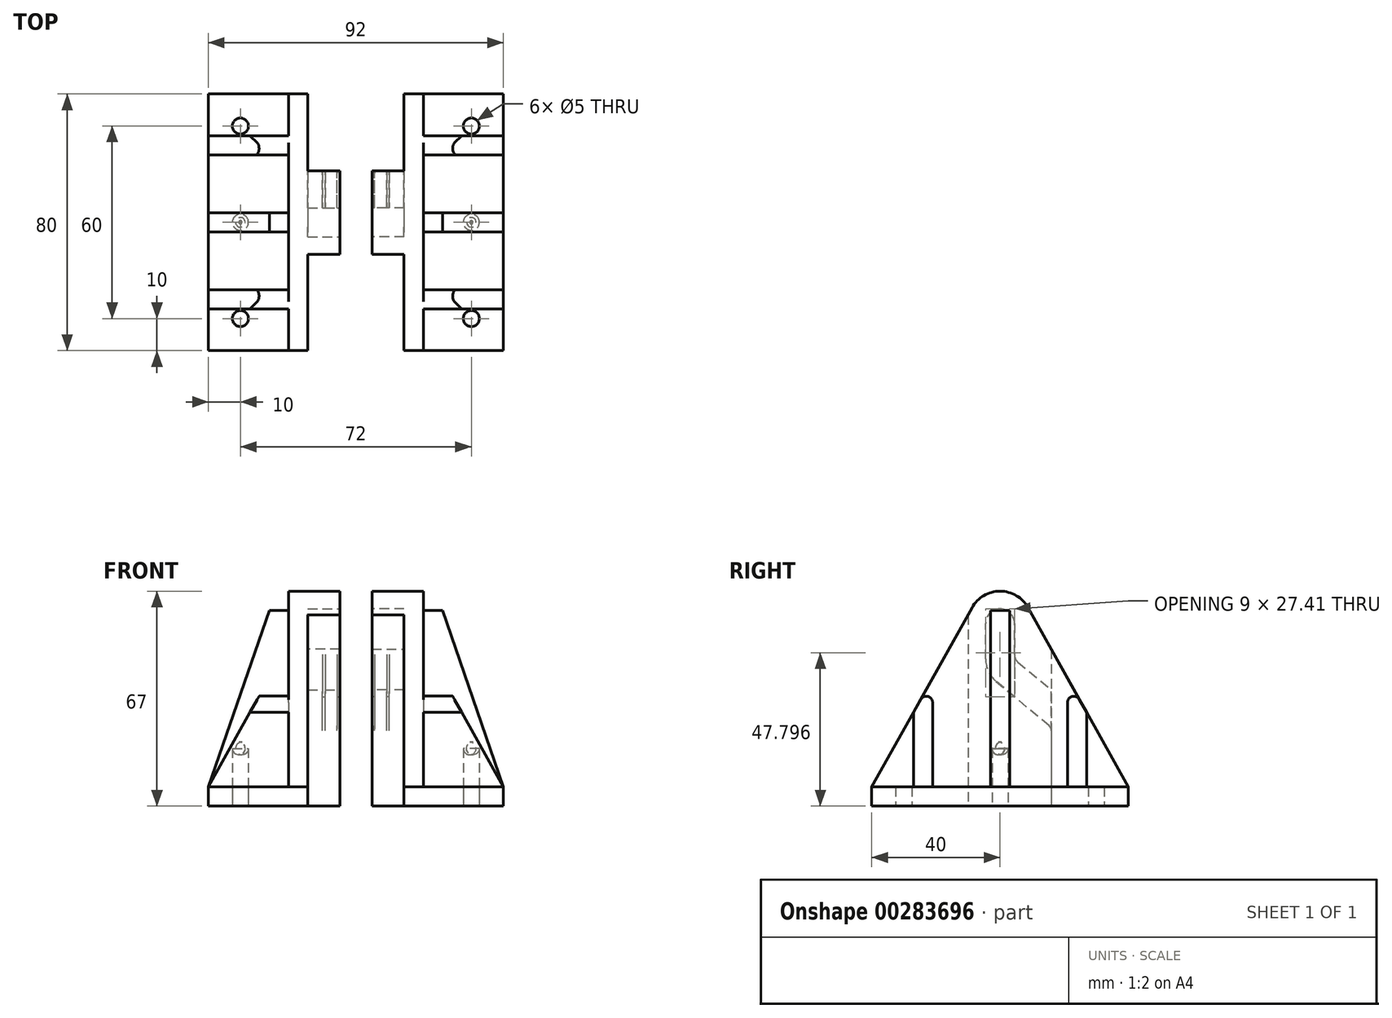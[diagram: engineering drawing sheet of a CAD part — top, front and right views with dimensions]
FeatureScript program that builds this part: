
annotation { "Feature Type Name" : "Feature", "Feature Type Description" : "" }
export const myFeature = defineFeature(function(context is Context, id is Id, definition is map)
    precondition{}
    {
        {
            var Q0;
            Q0=qCreatedBy(makeId("Top.planeOp"),FACE);
            var sketch = newSketch(context, id + "F0", { "sketchPlane" : qUnion([Q0])});
            skLineSegment(sketch, "E0.bottom", {"start": v(-15.5, 40) * mm, "end": v(15.5, 40) * mm});
            skLineSegment(sketch, "E0.top", {"start": v(-15.5, -40) * mm, "end": v(15.5, -40) * mm});
            skLineSegment(sketch, "E0.left", {"start": v(-15.5, 40) * mm, "end": v(-15.5, -40) * mm});
            skLineSegment(sketch, "E0.right", {"start": v(15.5, 40) * mm, "end": v(15.5, 16) * mm});
            skPoint(sketch, "E0.middle", {"position": v(0, 0) * mm});
            skLineSegment(sketch, "E1.bottom", {"start": v(15.5, 16) * mm, "end": v(25.5, 16) * mm});
            skLineSegment(sketch, "E1.top", {"start": v(15.5, -10) * mm, "end": v(25.5, -10) * mm});
            skLineSegment(sketch, "E1.right", {"start": v(25.5, 16) * mm, "end": v(25.5, -10) * mm});
            skLineSegment(sketch, "E2.trimOffspring", {"start": v(15.5, -10) * mm, "end": v(15.5, -40) * mm});
            skSolve(sketch);
        }
        {
            var Q0;
            Q0=makeQuery(id+"F0.imprint","IMPRINT",FACE,{"disambiguationData":[TD([[makeQuery(id+"F0.imprint","IMPRINT",EDGE,{"derivedFrom":sQuery(id+"F0.wireOp",EDGE,"E0.bottom")}),-1.0]])]});
            extrude(context, id + "F1", {"entities" : qUnion([Q0]), "depth" : 6 * mm});
        }
        {
            var Q0;
            Q0=makeQuery(id+"F1.opExtrude","CAP_FACE",FACE,{"disambiguationData":[OSD([sQuery(id+"F0.wireOp",EDGE,"E0.bottom"),sQuery(id+"F0.wireOp",EDGE,"E0.top"),sQuery(id+"F0.wireOp",EDGE,"E0.left"),sQuery(id+"F0.wireOp",EDGE,"E0.right"),sQuery(id+"F0.wireOp",EDGE,"E1.bottom"),sQuery(id+"F0.wireOp",EDGE,"E1.top"),sQuery(id+"F0.wireOp",EDGE,"E1.right"),sQuery(id+"F0.wireOp",EDGE,"E2.trimOffspring")])],"isStart":false});
            var sketch = newSketch(context, id + "F2", { "sketchPlane" : qUnion([Q0])});
            skLineSegment(sketch, "E3.bottom", {"start": v(15.5, 40) * mm, "end": v(9.5, 40) * mm});
            skLineSegment(sketch, "E3.top", {"start": v(15.5, -40) * mm, "end": v(9.5, -40) * mm});
            skLineSegment(sketch, "E3.left", {"start": v(15.5, 40) * mm, "end": v(15.5, -40) * mm});
            skLineSegment(sketch, "E3.right", {"start": v(9.5, 40) * mm, "end": v(9.5, -40) * mm});
            skSolve(sketch);
        }
        {
            var Q0;
            {var subQ3=sQuery(id+"F2.wireOp",EDGE,"E3.bottom");Q0=makeQuery(id+"F2.imprint","IMPRINT",FACE,{"disambiguationData":[TD([[makeQuery(id+"F2.imprint","IMPRINT",EDGE,{"derivedFrom":subQ3}),-1.0]])]});}
            extrude(context, id + "F3", {"entities" : qUnion([Q0]), "operationType" : NewBodyOperationType.ADD, "depth" : 61 * mm});
        }
        {
            var Q0;
            Q0=makeQuery(id+"F3.opExtrude","SWEPT_FACE",FACE,{"disambiguationData":[OSD([sQuery(id+"F2.wireOp",EDGE,"E3.right")])]});
            var sketch = newSketch(context, id + "F4", { "sketchPlane" : qUnion([Q0])});
            skCircle(sketch, "E4", {"center": v(0, 57) * mm, "radius": 4 * mm, "construction": true});
            skArc(sketch, "E5", {"start": v(8.73, 61.88) * mm, "mid": v(0, 67) * mm, "end": v(-8.73, 61.88) * mm});
            skLineSegment(sketch, "E6", {"start": v(-40, 6) * mm, "end": v(-8.73, 61.88) * mm});
            skLineSegment(sketch, "E7", {"start": v(40, 6) * mm, "end": v(8.73, 61.88) * mm});
            skLineSegment(sketch, "E8", {"start": v(-40, 6) * mm, "end": v(-55.29, 6) * mm});
            skLineSegment(sketch, "E9", {"start": v(-55.29, 6) * mm, "end": v(-55.29, 71.33) * mm});
            skLineSegment(sketch, "E10", {"start": v(-55.29, 71.33) * mm, "end": v(42.45, 71.33) * mm});
            skLineSegment(sketch, "E11", {"start": v(42.45, 71.33) * mm, "end": v(40, 6) * mm});
            skSolve(sketch);
        }
        {
            var Q0;
            Q0 = qSketchRegion(id + "F4", true);
            extrude(context, id + "F5", {"entities" : qUnion([Q0]), "operationType" : NewBodyOperationType.REMOVE, "oppositeDirection" : true, "depth" : 25 * mm});
        }
        {
            var Q0;
            {var subQ0=sQuery(id+"F0.wireOp",EDGE,"E0.left");var subQ1=sQuery(id+"F0.wireOp",EDGE,"E0.top");var subQ2=sQuery(id+"F0.wireOp",EDGE,"E0.bottom");Q0=makeQuery(id+"F3.boolean.opBoolean","SPLIT",FACE,{"disambiguationData":[TD([makeQuery(id+"F1.opExtrude","SWEPT_FACE",FACE,{"disambiguationData":[OSD([subQ2])]})])],"derivedFrom":makeQuery(id+"F1.opExtrude","CAP_FACE",FACE,{"disambiguationData":[OSD([subQ2,subQ1,subQ0,sQuery(id+"F0.wireOp",EDGE,"E0.right"),sQuery(id+"F0.wireOp",EDGE,"E1.bottom"),sQuery(id+"F0.wireOp",EDGE,"E1.top"),sQuery(id+"F0.wireOp",EDGE,"E1.right"),sQuery(id+"F0.wireOp",EDGE,"E2.trimOffspring")])],"isStart":false})});}
            var sketch = newSketch(context, id + "F6", { "sketchPlane" : qUnion([Q0])});
            skLineSegment(sketch, "E12.bottom", {"start": v(-15.5, 3) * mm, "end": v(9.5, 3) * mm});
            skLineSegment(sketch, "E12.top", {"start": v(-15.5, -3) * mm, "end": v(9.5, -3) * mm});
            skLineSegment(sketch, "E12.left", {"start": v(-15.5, 3) * mm, "end": v(-15.5, -3) * mm});
            skLineSegment(sketch, "E12.right", {"start": v(9.5, 3) * mm, "end": v(9.5, -3) * mm});
            skLineSegment(sketch, "E13.bottom", {"start": v(-15.5, -21) * mm, "end": v(9.5, -21) * mm});
            skLineSegment(sketch, "E13.top", {"start": v(-15.5, -27) * mm, "end": v(9.5, -27) * mm});
            skLineSegment(sketch, "E13.left", {"start": v(-15.5, -21) * mm, "end": v(-15.5, -27) * mm});
            skLineSegment(sketch, "E13.right", {"start": v(9.5, -21) * mm, "end": v(9.5, -27) * mm});
            skLineSegment(sketch, "E14.bottom", {"start": v(-15.5, 27) * mm, "end": v(9.5, 27) * mm});
            skLineSegment(sketch, "E14.top", {"start": v(-15.5, 21) * mm, "end": v(9.5, 21) * mm});
            skLineSegment(sketch, "E14.left", {"start": v(-15.5, 27) * mm, "end": v(-15.5, 21) * mm});
            skLineSegment(sketch, "E14.right", {"start": v(9.5, 27) * mm, "end": v(9.5, 21) * mm});
            skSolve(sketch);
        }
        {
            var Q0;
            Q0 = qSketchRegion(id + "F6", true);
            extrude(context, id + "F7", {"entities" : qUnion([Q0]), "operationType" : NewBodyOperationType.ADD, "depth" : 55 * mm});
        }
        {
            var Q0;
            Q0=makeQuery(id+"F7.opExtrude","SWEPT_FACE",FACE,{"disambiguationData":[OSD([sQuery(id+"F6.wireOp",EDGE,"E13.right")])]});
            var sketch = newSketch(context, id + "F8", { "sketchPlane" : qUnion([Q0])});
            skLineSegment(sketch, "E15.0", {"start": v(-40, 6) * mm, "end": v(-27, 29.23) * mm});
            skLineSegment(sketch, "E15.1", {"start": v(-27, 29.23) * mm, "end": v(-21, 39.95) * mm});
            skLineSegment(sketch, "E15.2", {"start": v(-21, 39.95) * mm, "end": v(-8.73, 61.88) * mm});
            skArc(sketch, "E15.3", {"start": v(-8.73, 61.88) * mm, "mid": v(-6.3, 64.76) * mm, "end": v(-3, 66.54) * mm});
            skArc(sketch, "E15.4", {"start": v(-3, 66.54) * mm, "mid": v(0, 67) * mm, "end": v(3, 66.54) * mm});
            skArc(sketch, "E15.5", {"start": v(3, 66.54) * mm, "mid": v(6.3, 64.76) * mm, "end": v(8.73, 61.88) * mm});
            skLineSegment(sketch, "E15.6", {"start": v(21, 39.95) * mm, "end": v(8.73, 61.88) * mm});
            skLineSegment(sketch, "E15.7", {"start": v(27, 29.23) * mm, "end": v(21, 39.95) * mm});
            skLineSegment(sketch, "E15.8", {"start": v(40, 6) * mm, "end": v(27, 29.23) * mm});
            skLineSegment(sketch, "E16", {"start": v(-40, 6) * mm, "end": v(-71.4, 87.62) * mm});
            skLineSegment(sketch, "E17", {"start": v(-71.4, 87.62) * mm, "end": v(67.9, 87.62) * mm});
            skLineSegment(sketch, "E18", {"start": v(67.9, 87.62) * mm, "end": v(40, 6) * mm});
            skSolve(sketch);
        }
        {
            var Q0;
            Q0 = qSketchRegion(id + "F8", true);
            extrude(context, id + "F9", {"entities" : qUnion([Q0]), "operationType" : NewBodyOperationType.REMOVE, "oppositeDirection" : true, "depth" : 66 * mm});
        }
        {
            var Q0;
            Q0=makeQuery(id+"F3.boolean.opBoolean","MERGE",FACE,{"derivedFrom":[makeQuery(id+"F1.opExtrude","SWEPT_FACE",FACE,{"disambiguationData":[OSD([sQuery(id+"F0.wireOp",EDGE,"E0.right")])]}),makeQuery(id+"F1.opExtrude","SWEPT_FACE",FACE,{"disambiguationData":[OSD([sQuery(id+"F0.wireOp",EDGE,"E2.trimOffspring")])]}),makeQuery(id+"F3.opExtrude","SWEPT_FACE",FACE,{"disambiguationData":[OSD([sQuery(id+"F2.wireOp",EDGE,"E3.left")])]})]});
            var sketch = newSketch(context, id + "F10", { "sketchPlane" : qUnion([Q0])});
            skLineSegment(sketch, "E19.bottom", {"start": v(-10, 6) * mm, "end": v(16, 6) * mm});
            skLineSegment(sketch, "E19.left", {"start": v(-10, 6) * mm, "end": v(-10, 59.6) * mm});
            skLineSegment(sketch, "E19.right", {"start": v(16, 6) * mm, "end": v(16, 48.89) * mm});
            skLineSegment(sketch, "E20.0", {"start": v(-8.73, 61.88) * mm, "end": v(-10, 59.6) * mm});
            skArc(sketch, "E20.1", {"start": v(8.73, 61.88) * mm, "mid": v(0, 67) * mm, "end": v(-8.73, 61.88) * mm});
            skLineSegment(sketch, "E20.2", {"start": v(8.73, 61.88) * mm, "end": v(16, 48.89) * mm});
            skPoint(sketch, "E21.orphan", {"position": v(-40, 6) * mm});
            skPoint(sketch, "E22.orphan", {"position": v(16, 73.46) * mm});
            skPoint(sketch, "E23.orphan", {"position": v(40, 6) * mm});
            skSolve(sketch);
        }
        {
            var Q0;
            Q0 = qSketchRegion(id + "F10", true);
            var Q1;
            Q1=makeQuery(id+"F1.opExtrude","SWEPT_FACE",FACE,{"disambiguationData":[OSD([sQuery(id+"F0.wireOp",EDGE,"E1.right")])]});
            extrude(context, id + "F11", {"entities" : qUnion([Q0]), "operationType" : NewBodyOperationType.ADD, "endBound" : BoundingType.UP_TO_SURFACE, "endBoundEntityFace" : qUnion([Q1]), "depth" : 25 * mm});
        }
        {
            var Q0;
            Q0=makeQuery(id+"F11.boolean.opBoolean","MERGE",FACE,{"derivedFrom":[makeQuery(id+"F1.opExtrude","SWEPT_FACE",FACE,{"disambiguationData":[OSD([sQuery(id+"F0.wireOp",EDGE,"E1.right")])]}),makeQuery(id+"F11.opExtrude","CAP_FACE",FACE,{"disambiguationData":[OSD([sQuery(id+"F10.wireOp",EDGE,"E19.bottom"),sQuery(id+"F10.wireOp",EDGE,"E19.left"),sQuery(id+"F10.wireOp",EDGE,"E19.right"),sQuery(id+"F10.wireOp",EDGE,"E20.0"),sQuery(id+"F10.wireOp",EDGE,"E20.1"),sQuery(id+"F10.wireOp",EDGE,"E20.2")])],"isStart":false})]});
            var sketch = newSketch(context, id + "F12", { "sketchPlane" : qUnion([Q0])});
            skLineSegment(sketch, "E24", {"start": v(-4.5, 57) * mm, "end": v(-4.5, 45.84) * mm});
            skLineSegment(sketch, "E25", {"start": v(-1.29, 38.95) * mm, "end": v(16, 24.44) * mm});
            skLineSegment(sketch, "E26", {"start": v(16, 36.2) * mm, "end": v(5.57, 44.94) * mm});
            skLineSegment(sketch, "E27", {"start": v(0, 61.5) * mm, "end": v(0, 61.5) * mm});
            skLineSegment(sketch, "E28", {"start": v(4.5, 57) * mm, "end": v(4.5, 47.24) * mm});
            skLineSegment(sketch, "E29", {"start": v(16, 36.2) * mm, "end": v(16, 24.44) * mm});
            skPoint(sketch, "E30.visualSharp", {"position": v(-4.5, 61.5) * mm});
            skArc(sketch, "E30.filletArc", {"start": v(0, 61.5) * mm, "mid": v(-3.18, 60.18) * mm, "end": v(-4.5, 57) * mm});
            skPoint(sketch, "E31.visualSharp", {"position": v(4.5, 61.5) * mm});
            skArc(sketch, "E31.filletArc", {"start": v(4.5, 57) * mm, "mid": v(3.18, 60.18) * mm, "end": v(0, 61.5) * mm});
            skPoint(sketch, "E32.visualSharp", {"position": v(-4.5, 41.64) * mm});
            skArc(sketch, "E32.filletArc", {"start": v(-4.5, 45.84) * mm, "mid": v(-3.66, 42.04) * mm, "end": v(-1.29, 38.95) * mm});
            skArc(sketch, "E33.filletArc", {"start": v(4.5, 47.24) * mm, "mid": v(4.78, 45.97) * mm, "end": v(5.57, 44.94) * mm});
            skSolve(sketch);
        }
        {
            var Q0;
            Q0 = qSketchRegion(id + "F12", true);
            var Q1;
            {var subQ0=sQuery(id+"F0.wireOp",EDGE,"E2.trimOffspring");var subQ2=sQuery(id+"F0.wireOp",EDGE,"E0.right");var subQ3=sQuery(id+"F0.wireOp",EDGE,"E0.bottom");Q1=makeQuery(id+"F11.boolean.opBoolean","SPLIT",FACE,{"disambiguationData":[TD([makeQuery(id+"F1.opExtrude","SWEPT_FACE",FACE,{"disambiguationData":[OSD([subQ3])]})])],"derivedFrom":makeQuery(id+"F3.boolean.opBoolean","MERGE",FACE,{"derivedFrom":[makeQuery(id+"F1.opExtrude","SWEPT_FACE",FACE,{"disambiguationData":[OSD([subQ2])]}),makeQuery(id+"F1.opExtrude","SWEPT_FACE",FACE,{"disambiguationData":[OSD([subQ0])]}),makeQuery(id+"F3.opExtrude","SWEPT_FACE",FACE,{"disambiguationData":[OSD([sQuery(id+"F2.wireOp",EDGE,"E3.left")])]})]})});}
            extrude(context, id + "F13", {"entities" : qUnion([Q0]), "operationType" : NewBodyOperationType.REMOVE, "endBound" : BoundingType.UP_TO_SURFACE, "oppositeDirection" : true, "endBoundEntityFace" : qUnion([Q1]), "depth" : 25 * mm});
        }
        {
            var Q0;
            Q0=makeQuery(id+"F13.boolean.opBoolean","COPY",EDGE,{"derivedFrom":makeQuery(id+"F13.opExtrude","SWEPT_EDGE",EDGE,{"disambiguationData":[OSD([sQuery(id+"F0.wireOp",EDGE,"E1.bottom"),sQuery(id+"F0.wireOp",EDGE,"E1.right"),sQuery(id+"F10.wireOp",EDGE,"E19.right"),sQuery(id+"F12.wireOp",EDGE,"E26"),sQuery(id+"F12.wireOp",EDGE,"E29")])]})});
            var Q1;
            Q1=makeQuery(id+"F13.boolean.opBoolean","COPY",EDGE,{"derivedFrom":makeQuery(id+"F13.opExtrude","SWEPT_EDGE",EDGE,{"disambiguationData":[OSD([sQuery(id+"F0.wireOp",EDGE,"E1.bottom"),sQuery(id+"F0.wireOp",EDGE,"E1.right"),sQuery(id+"F10.wireOp",EDGE,"E19.right"),sQuery(id+"F12.wireOp",EDGE,"E25"),sQuery(id+"F12.wireOp",EDGE,"E29")])]})});
            fillet(context, id + "F14", {"entities" : qUnion([Q0, Q1]), "radius" : 2 * mm, "tangentPropagation" : true, "allowEdgeOverflow" : false});
        }
        {
            var Q0;
            {var subQ0=sQuery(id+"F0.wireOp",EDGE,"E2.trimOffspring");var subQ2=sQuery(id+"F0.wireOp",EDGE,"E0.right");var subQ3=sQuery(id+"F0.wireOp",EDGE,"E0.bottom");Q0=makeQuery(id+"F13.boolean.opBoolean","MERGE",FACE,{"derivedFrom":[makeQuery(id+"F11.boolean.opBoolean","SPLIT",FACE,{"disambiguationData":[TD([makeQuery(id+"F1.opExtrude","SWEPT_FACE",FACE,{"disambiguationData":[OSD([subQ3])]})])],"derivedFrom":makeQuery(id+"F3.boolean.opBoolean","MERGE",FACE,{"derivedFrom":[makeQuery(id+"F1.opExtrude","SWEPT_FACE",FACE,{"disambiguationData":[OSD([subQ2])]}),makeQuery(id+"F1.opExtrude","SWEPT_FACE",FACE,{"disambiguationData":[OSD([subQ0])]}),makeQuery(id+"F3.opExtrude","SWEPT_FACE",FACE,{"disambiguationData":[OSD([sQuery(id+"F2.wireOp",EDGE,"E3.left")])]})]})})],"fromTools":[makeQuery(id+"F13.opExtrude","CAP_FACE",FACE,{"disambiguationData":[OSD([sQuery(id+"F12.wireOp",EDGE,"E24"),sQuery(id+"F12.wireOp",EDGE,"E25"),sQuery(id+"F12.wireOp",EDGE,"E26"),sQuery(id+"F12.wireOp",EDGE,"E28"),sQuery(id+"F12.wireOp",EDGE,"E29"),sQuery(id+"F12.wireOp",EDGE,"E30.filletArc"),sQuery(id+"F12.wireOp",EDGE,"E31.filletArc"),sQuery(id+"F12.wireOp",EDGE,"E32.filletArc"),sQuery(id+"F12.wireOp",EDGE,"E33.filletArc")])],"isStart":false})]});}
            cPlane(context, id + "F15", {"entities" : qUnion([Q0]), "cplaneType" : CPlaneType.OFFSET, "offset" : 5 * mm, "width" : 150 * mm, "height" : 150 * mm});
        }
        {
            var Q0;
            Q0=qCreatedBy(id+"F15.planeOp",FACE);
            var sketch = newSketch(context, id + "F16", { "sketchPlane" : qUnion([Q0])});
            skLineSegment(sketch, "E34", {"start": v(4.5, 50.13) * mm, "end": v(4.5, 33.16) * mm});
            skLineSegment(sketch, "E35", {"start": v(4.5, 33.16) * mm, "end": v(16, 23.51) * mm});
            skLineSegment(sketch, "E36", {"start": v(16, 23.51) * mm, "end": v(16, 40.48) * mm});
            skLineSegment(sketch, "E37", {"start": v(16, 40.48) * mm, "end": v(4.5, 50.13) * mm});
            skSolve(sketch);
        }
        {
            var Q0;
            Q0=makeQuery(id+"F16.imprint","IMPRINT",FACE,{"disambiguationData":[TD([[makeQuery(id+"F16.imprint","IMPRINT",EDGE,{"derivedFrom":sQuery(id+"F16.wireOp",EDGE,"E34")}),1.0]])]});
            extrude(context, id + "F17", {"entities" : qUnion([Q0]), "operationType" : NewBodyOperationType.ADD, "depth" : 0.4 * mm, "hasSecondDirection" : true, "secondDirectionOppositeDirection" : true, "secondDirectionDepth" : 0.4 * mm});
        }
        {
            var Q0;
            Q0=makeQuery(id+"F11.boolean.opBoolean","MERGE",FACE,{"derivedFrom":[makeQuery(id+"F1.opExtrude","SWEPT_FACE",FACE,{"disambiguationData":[OSD([sQuery(id+"F0.wireOp",EDGE,"E1.right")])]}),makeQuery(id+"F11.opExtrude","CAP_FACE",FACE,{"disambiguationData":[OSD([sQuery(id+"F10.wireOp",EDGE,"E19.bottom"),sQuery(id+"F10.wireOp",EDGE,"E19.left"),sQuery(id+"F10.wireOp",EDGE,"E19.right"),sQuery(id+"F10.wireOp",EDGE,"E20.0"),sQuery(id+"F10.wireOp",EDGE,"E20.1"),sQuery(id+"F10.wireOp",EDGE,"E20.2")])],"isStart":false})]});
            var sketch = newSketch(context, id + "F18", { "sketchPlane" : qUnion([Q0])});
            skLineSegment(sketch, "E38.0.0", {"start": v(12.71, 38.95) * mm, "end": v(5.57, 44.94) * mm});
            skArc(sketch, "E38.0.1", {"start": v(5.57, 44.94) * mm, "mid": v(4.78, 45.97) * mm, "end": v(4.5, 47.24) * mm});
            skLineSegment(sketch, "E38.0.2", {"start": v(4.5, 47.24) * mm, "end": v(4.5, 34.1) * mm});
            skLineSegment(sketch, "E38.0.3", {"start": v(4.5, 34.1) * mm, "end": v(15.29, 25.04) * mm});
            skArc(sketch, "E38.0.4", {"start": v(15.29, 25.04) * mm, "mid": v(15.81, 24.36) * mm, "end": v(16, 23.51) * mm});
            skLineSegment(sketch, "E38.0.5", {"start": v(16, 23.51) * mm, "end": v(16, 40.48) * mm});
            skArc(sketch, "E38.0.6", {"start": v(16, 40.48) * mm, "mid": v(14.85, 38.67) * mm, "end": v(12.71, 38.95) * mm});
            skSolve(sketch);
        }
        {
            var Q0;
            Q0 = qSketchRegion(id + "F18", true);
            extrude(context, id + "F19", {"entities" : qUnion([Q0]), "operationType" : NewBodyOperationType.ADD, "oppositeDirection" : true, "depth" : 0.8 * mm});
        }
        {
            var Q0;
            Q0=makeQuery(id+"F1.opExtrude","CAP_FACE",FACE,{"disambiguationData":[OSD([sQuery(id+"F0.wireOp",EDGE,"E0.bottom"),sQuery(id+"F0.wireOp",EDGE,"E0.top"),sQuery(id+"F0.wireOp",EDGE,"E0.left"),sQuery(id+"F0.wireOp",EDGE,"E0.right"),sQuery(id+"F0.wireOp",EDGE,"E1.bottom"),sQuery(id+"F0.wireOp",EDGE,"E1.top"),sQuery(id+"F0.wireOp",EDGE,"E1.right"),sQuery(id+"F0.wireOp",EDGE,"E2.trimOffspring")])],"isStart":true});
            var sketch = newSketch(context, id + "F20", { "sketchPlane" : qUnion([Q0])});
            skCircle(sketch, "E39", {"center": v(-5.5, 0) * mm, "radius": 2.5 * mm});
            skCircle(sketch, "E40", {"center": v(-5.5, 30) * mm, "radius": 2.5 * mm});
            skCircle(sketch, "E41", {"center": v(-5.5, -30) * mm, "radius": 2.5 * mm});
            skSolve(sketch);
        }
        {
            var Q0;
            Q0 = qSketchRegion(id + "F20", true);
            extrude(context, id + "F21", {"entities" : qUnion([Q0]), "operationType" : NewBodyOperationType.REMOVE, "oppositeDirection" : true, "depth" : 20 * mm});
        }
        {
            var Q0;
            Q0=makeQuery(id+"F21.boolean.opBoolean","COPY",EDGE,{"derivedFrom":makeQuery(id+"F21.opExtrude","CAP_EDGE",EDGE,{"disambiguationData":[OSD([sQuery(id+"F20.wireOp",EDGE,"E39")])],"isStart":false})});
            fillet(context, id + "F22", {"entities" : qUnion([Q0]), "radius" : 2 * mm, "tangentPropagation" : true, "allowEdgeOverflow" : false});
        }
        {
            var Q0;
            Q0=makeQuery(id+"F7.opExtrude","SWEPT_FACE",FACE,{"disambiguationData":[OSD([sQuery(id+"F6.wireOp",EDGE,"E13.top")])]});
            var sketch = newSketch(context, id + "F23", { "sketchPlane" : qUnion([Q0])});
            skLineSegment(sketch, "E42", {"start": v(9.5, 39.95) * mm, "end": v(3.5, 39.95) * mm});
            skPoint(sketch, "E42.startSnap0", {"position": v(9.5, 17.62) * mm});
            skLineSegment(sketch, "E43", {"start": v(3.5, 39.95) * mm, "end": v(-15.5, 6) * mm});
            skLineSegment(sketch, "E44", {"start": v(-15.5, 6) * mm, "end": v(-37.9, 6) * mm});
            skLineSegment(sketch, "E45", {"start": v(-37.9, 6) * mm, "end": v(-37.9, 46.4) * mm});
            skLineSegment(sketch, "E46", {"start": v(-37.9, 46.4) * mm, "end": v(9.5, 46.4) * mm});
            skLineSegment(sketch, "E47", {"start": v(9.5, 46.4) * mm, "end": v(9.5, 39.95) * mm});
            skSolve(sketch);
        }
        {
            var Q0;
            Q0 = qSketchRegion(id + "F23", true);
            extrude(context, id + "F24", {"entities" : qUnion([Q0]), "operationType" : NewBodyOperationType.REMOVE, "oppositeDirection" : true, "depth" : 14.1 * mm});
        }
        {
            var Q0;
            Q0=makeQuery(id+"F7.opExtrude","SWEPT_FACE",FACE,{"disambiguationData":[OSD([sQuery(id+"F6.wireOp",EDGE,"E14.bottom")])]});
            var sketch = newSketch(context, id + "F25", { "sketchPlane" : qUnion([Q0])});
            skLineSegment(sketch, "E48", {"start": v(-9.5, 39.95) * mm, "end": v(-3.5, 39.95) * mm});
            skLineSegment(sketch, "E49", {"start": v(-3.5, 39.95) * mm, "end": v(15.5, 6) * mm});
            skLineSegment(sketch, "E50", {"start": v(15.5, 6) * mm, "end": v(21, 6) * mm});
            skLineSegment(sketch, "E51", {"start": v(21, 6) * mm, "end": v(21, 49.57) * mm});
            skLineSegment(sketch, "E52", {"start": v(21, 49.57) * mm, "end": v(-9.5, 49.57) * mm});
            skLineSegment(sketch, "E53", {"start": v(-9.5, 49.57) * mm, "end": v(-9.5, 39.95) * mm});
            skSolve(sketch);
        }
        {
            var Q0;
            Q0 = qSketchRegion(id + "F25", true);
            extrude(context, id + "F26", {"entities" : qUnion([Q0]), "operationType" : NewBodyOperationType.REMOVE, "oppositeDirection" : true, "depth" : 9.9 * mm});
        }
        {
            var Q0;
            Q0=makeQuery(id+"F7.opExtrude","SWEPT_FACE",FACE,{"disambiguationData":[OSD([sQuery(id+"F6.wireOp",EDGE,"E12.bottom")])]});
            var sketch = newSketch(context, id + "F27", { "sketchPlane" : qUnion([Q0])});
            skLineSegment(sketch, "E54", {"start": v(-9.5, 61) * mm, "end": v(-3.5, 61) * mm});
            skLineSegment(sketch, "E55", {"start": v(-3.5, 61) * mm, "end": v(15.5, 6) * mm});
            skLineSegment(sketch, "E56", {"start": v(15.5, 6) * mm, "end": v(33.5, 48.33) * mm});
            skLineSegment(sketch, "E57", {"start": v(33.5, 48.33) * mm, "end": v(22.29, 65.74) * mm});
            skLineSegment(sketch, "E58", {"start": v(22.29, 65.74) * mm, "end": v(-9.5, 63.87) * mm});
            skLineSegment(sketch, "E59", {"start": v(-9.5, 63.87) * mm, "end": v(-9.5, 61) * mm});
            skSolve(sketch);
        }
        {
            var Q0;
            Q0 = qSketchRegion(id + "F27", true);
            extrude(context, id + "F28", {"entities" : qUnion([Q0]), "operationType" : NewBodyOperationType.REMOVE, "oppositeDirection" : true, "depth" : 6.1 * mm});
        }
        {
            var Q0;
            Q0=makeQuery(id+"F9.boolean.opBoolean","INTERSECT",EDGE,{"derivedFrom":[makeQuery(id+"F7.opExtrude","SWEPT_FACE",FACE,{"disambiguationData":[OSD([sQuery(id+"F6.wireOp",EDGE,"E14.top")])]}),makeQuery(id+"F9.opExtrude","SWEPT_FACE",FACE,{"disambiguationData":[OSD([sQuery(id+"F8.wireOp",EDGE,"E15.6"),sQuery(id+"F8.wireOp",EDGE,"E15.7"),sQuery(id+"F8.wireOp",EDGE,"E15.8")])]})]});
            var Q1;
            Q1=makeQuery(id+"F9.boolean.opBoolean","INTERSECT",EDGE,{"derivedFrom":[makeQuery(id+"F7.opExtrude","SWEPT_FACE",FACE,{"disambiguationData":[OSD([sQuery(id+"F6.wireOp",EDGE,"E13.bottom")])]}),makeQuery(id+"F9.opExtrude","SWEPT_FACE",FACE,{"disambiguationData":[OSD([sQuery(id+"F8.wireOp",EDGE,"E15.0"),sQuery(id+"F8.wireOp",EDGE,"E15.1"),sQuery(id+"F8.wireOp",EDGE,"E15.2")])]})]});
            fillet(context, id + "F29", {"entities" : qUnion([Q0, Q1]), "radius" : 2 * mm, "tangentPropagation" : true, "allowEdgeOverflow" : false});
        }
        {
            var Q0;
            Q0=makeQuery(id+"F19.boolean.opBoolean","MERGE",FACE,{"derivedFrom":[makeQuery(id+"F11.boolean.opBoolean","MERGE",FACE,{"derivedFrom":[makeQuery(id+"F1.opExtrude","SWEPT_FACE",FACE,{"disambiguationData":[OSD([sQuery(id+"F0.wireOp",EDGE,"E1.right")])]}),makeQuery(id+"F11.opExtrude","CAP_FACE",FACE,{"disambiguationData":[OSD([sQuery(id+"F10.wireOp",EDGE,"E19.bottom"),sQuery(id+"F10.wireOp",EDGE,"E19.left"),sQuery(id+"F10.wireOp",EDGE,"E19.right"),sQuery(id+"F10.wireOp",EDGE,"E20.0"),sQuery(id+"F10.wireOp",EDGE,"E20.1"),sQuery(id+"F10.wireOp",EDGE,"E20.2")])],"isStart":false})]}),makeQuery(id+"F19.opExtrude","CAP_FACE",FACE,{"disambiguationData":[OSD([sQuery(id+"F18.wireOp",EDGE,"E38.0.0"),sQuery(id+"F18.wireOp",EDGE,"E38.0.1"),sQuery(id+"F18.wireOp",EDGE,"E38.0.2"),sQuery(id+"F18.wireOp",EDGE,"E38.0.3"),sQuery(id+"F18.wireOp",EDGE,"E38.0.4"),sQuery(id+"F18.wireOp",EDGE,"E38.0.5"),sQuery(id+"F18.wireOp",EDGE,"E38.0.6")])],"isStart":true})]});
            cPlane(context, id + "F30", {"entities" : qUnion([Q0]), "cplaneType" : CPlaneType.OFFSET, "offset" : 5 * mm, "width" : 150 * mm, "height" : 150 * mm});
        }
        {
            var Q0;
            Q0=makeQuery(id+"F1.opExtrude","SWEPT_BODY",BODY,{"disambiguationData":[OSD([sQuery(id+"F0.wireOp",EDGE,"E0.bottom"),sQuery(id+"F0.wireOp",EDGE,"E0.top"),sQuery(id+"F0.wireOp",EDGE,"E0.left"),sQuery(id+"F0.wireOp",EDGE,"E0.right"),sQuery(id+"F0.wireOp",EDGE,"E1.bottom"),sQuery(id+"F0.wireOp",EDGE,"E1.top"),sQuery(id+"F0.wireOp",EDGE,"E1.right"),sQuery(id+"F0.wireOp",EDGE,"E2.trimOffspring")])]});
            var Q1;
            Q1=qCreatedBy(id+"F30.planeOp",FACE);
            mirror(context, id + "F31", {"entities" : qUnion([Q0]), "mirrorPlane" : qUnion([Q1])});
        }
    });
